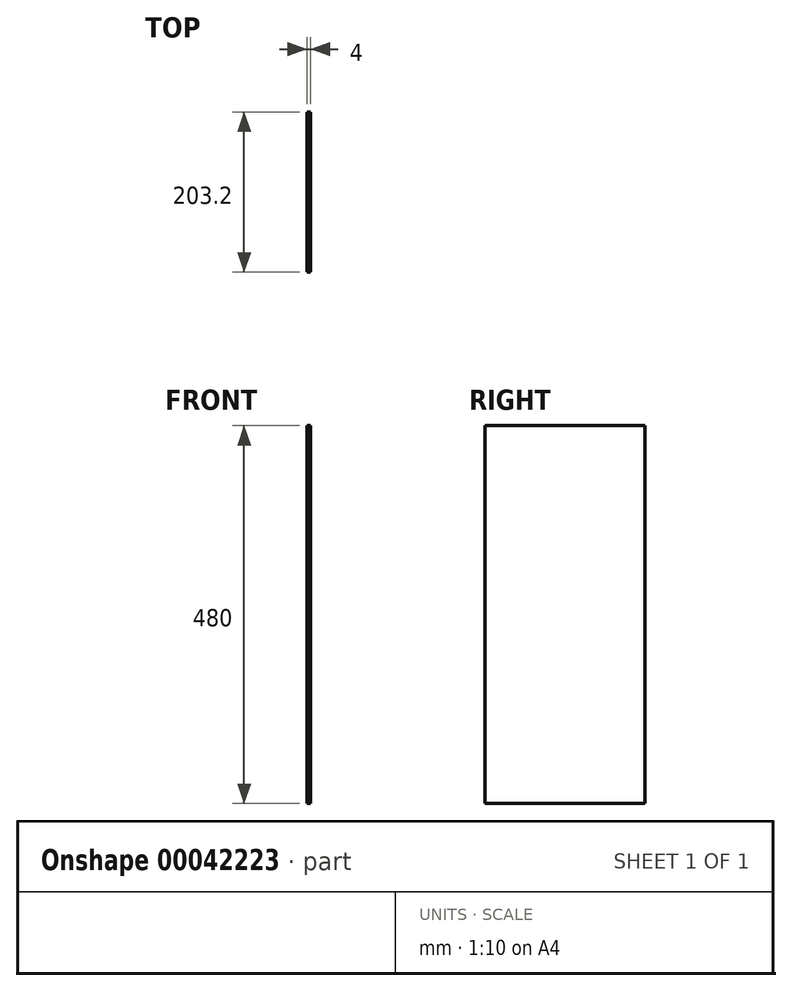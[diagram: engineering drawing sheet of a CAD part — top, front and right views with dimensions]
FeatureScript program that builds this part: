
annotation { "Feature Type Name" : "Feature", "Feature Type Description" : "" }
export const myFeature = defineFeature(function(context is Context, id is Id, definition is map)
    precondition{}
    {
        {
            var Q0;
            Q0=qCreatedBy(makeId("Right.planeOp"),FACE);
            var sketch = newSketch(context, id + "F0", { "sketchPlane" : qUnion([Q0])});
            skLineSegment(sketch, "E0.rect.bottom", {"start": v(-101.6, 240) * mm, "end": v(101.6, 240) * mm});
            skLineSegment(sketch, "E0.rect.top", {"start": v(-101.6, -240) * mm, "end": v(101.6, -240) * mm});
            skLineSegment(sketch, "E0.rect.left", {"start": v(-101.6, 240) * mm, "end": v(-101.6, -240) * mm});
            skLineSegment(sketch, "E0.rect.right", {"start": v(101.6, 240) * mm, "end": v(101.6, -240) * mm});
            skPoint(sketch, "E0.rect.middle", {"position": v(0, 0) * mm});
            skSolve(sketch);
        }
        {
            var Q0;
            Q0=makeQuery(id+"F0.imprint","IMPRINT",FACE,{"disambiguationData":[TD([[makeQuery(id+"F0.imprint","IMPRINT",EDGE,{"derivedFrom":sQuery(id+"F0.wireOp",EDGE,"E0.rect.bottom")}),-1.0]])]});
            extrude(context, id + "F1", {"entities" : qUnion([Q0]), "depth" : 4 * mm});
        }
    });
